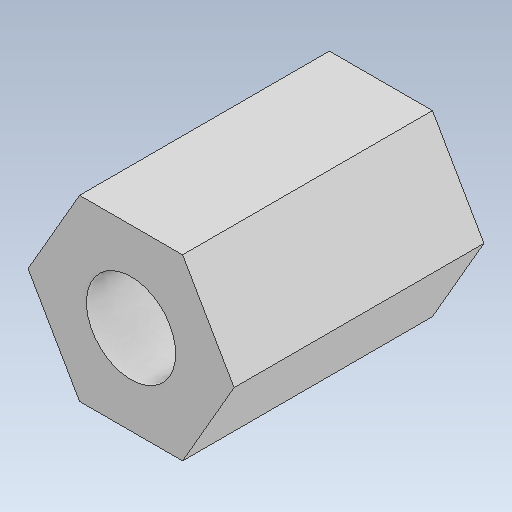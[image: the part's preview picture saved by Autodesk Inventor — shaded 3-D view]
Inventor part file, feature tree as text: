
AUTODESK INVENTOR PART (.ipt)
format: ipt  version: 2021 (Build 250183000, 183)  size: 99,328 bytes
history: native  units: mm
features: extrude x2, sketch x2
ambient origin geometry x8: Origin, YZ Plane, XZ Plane, XY Plane, X Axis, Y Axis, Z Axis, Center Point
bodies: Solid1 (feature_tree)
feature tree (4):
  extrude  "Extrusion1"  Depth=7.0mm TaperAngle=0.0deg
  extrude  "Extrusion3"  Depth=7.0mm TaperAngle=0.0deg
  sketch  "Sketch1"  dims[d0=5.0mm d1=7.0mm d2=0.0mm]
  sketch  "Sketch3"  dims[d6=2.5mm d7=7.0mm d8=0.0mm]
